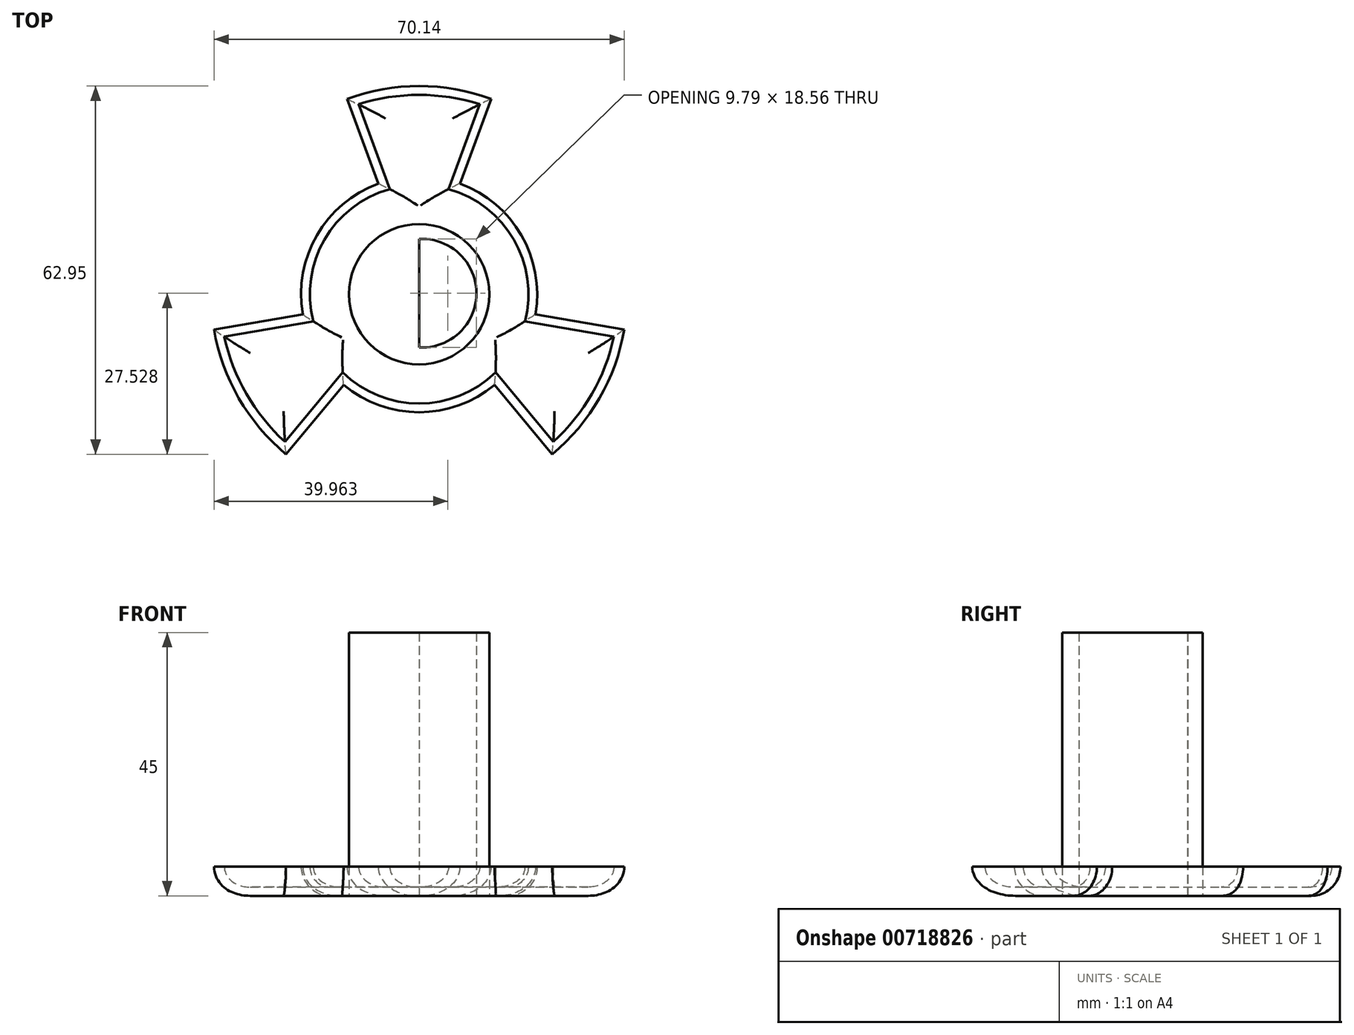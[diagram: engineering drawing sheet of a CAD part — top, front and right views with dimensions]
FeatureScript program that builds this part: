
annotation { "Feature Type Name" : "Feature", "Feature Type Description" : "" }
export const myFeature = defineFeature(function(context is Context, id is Id, definition is map)
    precondition{}
    {
        {
            var Q0;
            Q0=qCreatedBy(makeId("Top.planeOp"),FACE);
            var sketch = newSketch(context, id + "F0", { "sketchPlane" : qUnion([Q0])});
            skArc(sketch, "E0", {"start": v(12.3, 33.4) * mm, "mid": v(0, 35.59) * mm, "end": v(-12.3, 33.4) * mm});
            skArc(sketch, "E1", {"start": v(-6.98, 18.93) * mm, "mid": v(-17.47, 10.09) * mm, "end": v(-19.88, -3.42) * mm});
            skLineSegment(sketch, "E2", {"start": v(0, 35.59) * mm, "end": v(0, 0) * mm, "construction": true});
            skLineSegment(sketch, "E3", {"start": v(-12.3, 33.4) * mm, "end": v(-6.98, 18.93) * mm});
            skLineSegment(sketch, "E4.MirrorCS", {"start": v(12.3, 33.4) * mm, "end": v(6.98, 18.93) * mm});
            skArc(sketch, "E5.1.0", {"start": v(-35.07, -6.03) * mm, "mid": v(-30.82, -17.8) * mm, "end": v(-22.76, -27.36) * mm});
            skLineSegment(sketch, "E5.1.1", {"start": v(-22.76, -27.36) * mm, "end": v(-12.9, -15.5) * mm});
            skLineSegment(sketch, "E5.1.2", {"start": v(-35.07, -6.03) * mm, "end": v(-19.88, -3.42) * mm});
            skArc(sketch, "E5.2.0", {"start": v(22.76, -27.36) * mm, "mid": v(30.82, -17.8) * mm, "end": v(35.07, -6.03) * mm});
            skLineSegment(sketch, "E5.2.1", {"start": v(35.07, -6.03) * mm, "end": v(19.88, -3.42) * mm});
            skLineSegment(sketch, "E5.2.2", {"start": v(22.76, -27.36) * mm, "end": v(12.9, -15.5) * mm});
            skArc(sketch, "E6.trimOffspring", {"start": v(-12.9, -15.5) * mm, "mid": v(0, -20.18) * mm, "end": v(12.9, -15.5) * mm});
            skArc(sketch, "E7.trimOffspring", {"start": v(19.88, -3.42) * mm, "mid": v(17.47, 10.09) * mm, "end": v(6.98, 18.93) * mm});
            skSolve(sketch);
        }
        {
            var Q0;
            Q0=makeQuery(id+"F0.imprint","IMPRINT",FACE,{"disambiguationData":[TD([[makeQuery(id+"F0.imprint","IMPRINT",EDGE,{"derivedFrom":sQuery(id+"F0.wireOp",EDGE,"E0")}),1.0]])]});
            extrude(context, id + "F1", {"entities" : qUnion([Q0]), "depth" : 5 * mm, "offsetDistance" : 25 * mm});
        }
        {
            var Q0;
            Q0=makeQuery(id+"F1.opExtrude","CAP_FACE",FACE,{"disambiguationData":[OSD([sQuery(id+"F0.wireOp",EDGE,"E0"),sQuery(id+"F0.wireOp",EDGE,"E1"),sQuery(id+"F0.wireOp",EDGE,"E3"),sQuery(id+"F0.wireOp",EDGE,"E4.MirrorCS"),sQuery(id+"F0.wireOp",EDGE,"E5.1.0"),sQuery(id+"F0.wireOp",EDGE,"E5.1.1"),sQuery(id+"F0.wireOp",EDGE,"E5.1.2"),sQuery(id+"F0.wireOp",EDGE,"E5.2.0"),sQuery(id+"F0.wireOp",EDGE,"E5.2.1"),sQuery(id+"F0.wireOp",EDGE,"E5.2.2"),sQuery(id+"F0.wireOp",EDGE,"E6.trimOffspring"),sQuery(id+"F0.wireOp",EDGE,"E7.trimOffspring")])],"isStart":false});
            var sketch = newSketch(context, id + "F2", { "sketchPlane" : qUnion([Q0])});
            skCircle(sketch, "E8", {"center": v(0, 0) * mm, "radius": 12 * mm});
            skArc(sketch, "E9", {"start": v(0, -9.11) * mm, "mid": v(9.79, 0.17) * mm, "end": v(0, 9.45) * mm});
            skLineSegment(sketch, "E10", {"start": v(0, 9.45) * mm, "end": v(0, -9.11) * mm});
            skSolve(sketch);
        }
        {
            var Q0;
            Q0=makeQuery(id+"F2.imprint","IMPRINT",FACE,{"disambiguationData":[TD([[makeQuery(id+"F2.imprint","IMPRINT",EDGE,{"derivedFrom":sQuery(id+"F2.wireOp",EDGE,"E8")}),1.0]])]});
            extrude(context, id + "F3", {"entities" : qUnion([Q0]), "depth" : 40 * mm, "offsetDistance" : 25 * mm, "hasSecondDirection" : true, "secondDirectionOppositeDirection" : true, "secondDirectionDepth" : 5 * mm});
        }
        {
            var Q0;
            Q0=makeQuery(id+"F1.opExtrude","CAP_FACE",FACE,{"disambiguationData":[OSD([sQuery(id+"F0.wireOp",EDGE,"E0"),sQuery(id+"F0.wireOp",EDGE,"E1"),sQuery(id+"F0.wireOp",EDGE,"E3"),sQuery(id+"F0.wireOp",EDGE,"E4.MirrorCS"),sQuery(id+"F0.wireOp",EDGE,"E5.1.0"),sQuery(id+"F0.wireOp",EDGE,"E5.1.1"),sQuery(id+"F0.wireOp",EDGE,"E5.1.2"),sQuery(id+"F0.wireOp",EDGE,"E5.2.0"),sQuery(id+"F0.wireOp",EDGE,"E5.2.1"),sQuery(id+"F0.wireOp",EDGE,"E5.2.2"),sQuery(id+"F0.wireOp",EDGE,"E6.trimOffspring"),sQuery(id+"F0.wireOp",EDGE,"E7.trimOffspring")])],"isStart":true});
            fillet(context, id + "F4", {"entities" : qUnion([Q0]), "radius" : 5 * mm, "tangentPropagation" : true, "allowEdgeOverflow" : false});
        }
        {
            var Q0;
            Q0=makeQuery(id+"F1.opExtrude","CAP_FACE",FACE,{"disambiguationData":[OSD([sQuery(id+"F0.wireOp",EDGE,"E0"),sQuery(id+"F0.wireOp",EDGE,"E1"),sQuery(id+"F0.wireOp",EDGE,"E3"),sQuery(id+"F0.wireOp",EDGE,"E4.MirrorCS"),sQuery(id+"F0.wireOp",EDGE,"E5.1.0"),sQuery(id+"F0.wireOp",EDGE,"E5.1.1"),sQuery(id+"F0.wireOp",EDGE,"E5.1.2"),sQuery(id+"F0.wireOp",EDGE,"E5.2.0"),sQuery(id+"F0.wireOp",EDGE,"E5.2.1"),sQuery(id+"F0.wireOp",EDGE,"E5.2.2"),sQuery(id+"F0.wireOp",EDGE,"E6.trimOffspring"),sQuery(id+"F0.wireOp",EDGE,"E7.trimOffspring")])],"isStart":false});
            shell(context, id + "F5", {"entities" : qUnion([Q0]), "thickness" : 1.5 * mm});
        }
    });
